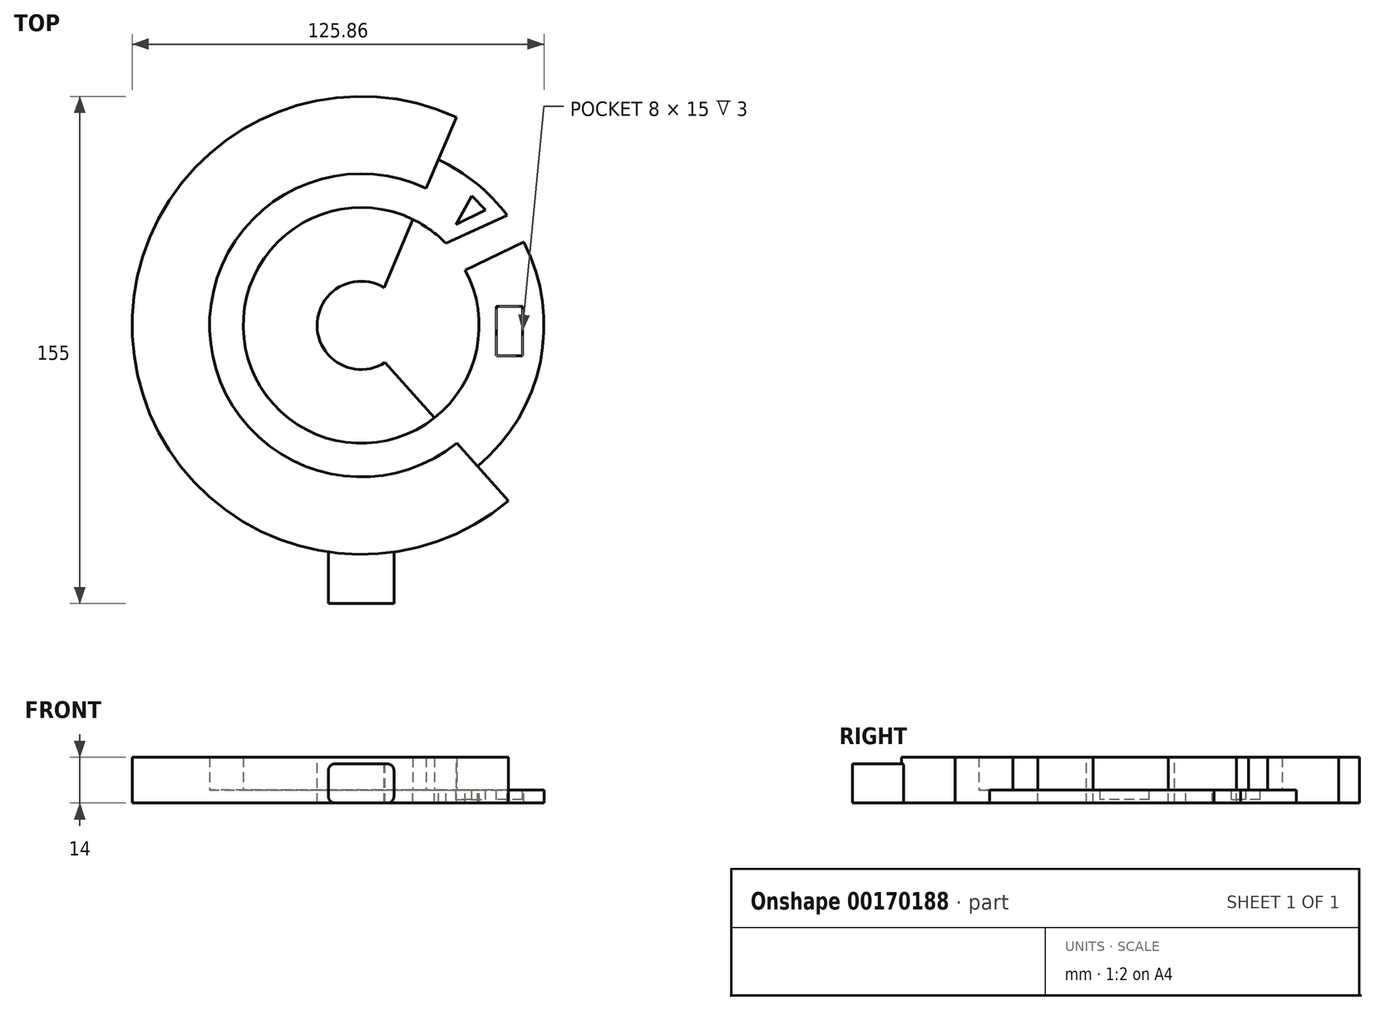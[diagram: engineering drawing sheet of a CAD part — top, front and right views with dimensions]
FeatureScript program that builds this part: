
annotation { "Feature Type Name" : "Feature", "Feature Type Description" : "" }
export const myFeature = defineFeature(function(context is Context, id is Id, definition is map)
    precondition{}
    {
        {
            var Q0;
            Q0=qCreatedBy(makeId("Top.planeOp"),FACE);
            var sketch = newSketch(context, id + "F0", { "sketchPlane" : qUnion([Q0])});
            skCircle(sketch, "E0", {"center": v(0, 0) * mm, "radius": 70 * mm});
            skCircle(sketch, "E1", {"center": v(0, 0) * mm, "radius": 46.34 * mm});
            skCircle(sketch, "E2", {"center": v(0, 0) * mm, "radius": 36.04 * mm});
            skCircle(sketch, "E3", {"center": v(0, 0) * mm, "radius": 13.49 * mm});
            skLineSegment(sketch, "E4", {"start": v(7.26, -11.37) * mm, "end": v(45, -53.62) * mm});
            skLineSegment(sketch, "E5", {"start": v(6.97, 11.55) * mm, "end": v(29.14, 63.65) * mm});
            skCircle(sketch, "E6", {"center": v(0, 0) * mm, "radius": 55.86 * mm});
            skCircle(sketch, "E7", {"center": v(0, 0) * mm, "radius": 32.82 * mm});
            skCircle(sketch, "E8", {"center": v(0, 0) * mm, "radius": 74.95 * mm});
            skLineSegment(sketch, "E9", {"start": v(26.8, -18.95) * mm, "end": v(42.53, -36.22) * mm});
            skLineSegment(sketch, "E10", {"start": v(49.72, 25.46) * mm, "end": v(28.92, 15.51) * mm});
            skLineSegment(sketch, "E11", {"start": v(22.75, 23.65) * mm, "end": v(40.37, 63.15) * mm});
            skLineSegment(sketch, "E12", {"start": v(22.75, 23.65) * mm, "end": v(62.3, 41.68) * mm});
            skLineSegment(sketch, "E13", {"start": v(0, -85) * mm, "end": v(0, -70) * mm});
            skLineSegment(sketch, "E14", {"start": v(0, -85) * mm, "end": v(10, -85) * mm});
            skLineSegment(sketch, "E15", {"start": v(0, -85) * mm, "end": v(-10, -85) * mm});
            skLineSegment(sketch, "E16", {"start": v(10, -85) * mm, "end": v(10, -69.28) * mm});
            skLineSegment(sketch, "E17", {"start": v(-10, -85) * mm, "end": v(-10, -69.28) * mm});
            skSolve(sketch);
        }
        {
            var Q0;
            {var subQ0=sQuery(id+"F0.wireOp",EDGE,"E4");var subQ1=sQuery(id+"F0.wireOp",EDGE,"E0");var subQ2=makeQuery(id+"F0.imprint","INTERSECT",VERTEX,{"derivedFrom":[subQ1,subQ0]});Q0=makeQuery(id+"F0.imprint","IMPRINT",FACE,{"disambiguationData":[TD([[makeQuery(id+"F0.imprint","IMPRINT",EDGE,{"disambiguationData":[TD([[subQ2,1.0]])],"derivedFrom":subQ1}),1.0]])]});}
            var Q1;
            {var subQ0=sQuery(id+"F0.wireOp",EDGE,"E5");var subQ1=sQuery(id+"F0.wireOp",EDGE,"E1");var subQ2=makeQuery(id+"F0.imprint","INTERSECT",VERTEX,{"derivedFrom":[subQ1,subQ0]});Q1=makeQuery(id+"F0.imprint","IMPRINT",FACE,{"disambiguationData":[TD([[makeQuery(id+"F0.imprint","IMPRINT",EDGE,{"disambiguationData":[TD([[subQ2,-1.0]])],"derivedFrom":subQ1}),-1.0]])]});}
            var Q2;
            {var subQ0=sQuery(id+"F0.wireOp",EDGE,"E5");var subQ1=sQuery(id+"F0.wireOp",EDGE,"E2");var subQ2=makeQuery(id+"F0.imprint","INTERSECT",VERTEX,{"derivedFrom":[subQ1,subQ0]});Q2=makeQuery(id+"F0.imprint","IMPRINT",FACE,{"disambiguationData":[TD([[makeQuery(id+"F0.imprint","IMPRINT",EDGE,{"disambiguationData":[TD([[subQ2,-1.0]])],"derivedFrom":subQ1}),1.0]])]});}
            var Q3;
            {var subQ0=sQuery(id+"F0.wireOp",EDGE,"E4");var subQ1=sQuery(id+"F0.wireOp",EDGE,"E3");var subQ2=makeQuery(id+"F0.imprint","INTERSECT",VERTEX,{"derivedFrom":[subQ1,subQ0]});Q3=makeQuery(id+"F0.imprint","IMPRINT",FACE,{"disambiguationData":[TD([[makeQuery(id+"F0.imprint","IMPRINT",EDGE,{"disambiguationData":[TD([[subQ2,1.0]])],"derivedFrom":subQ1}),-1.0]])]});}
            var Q4;
            {var subQ0=sQuery(id+"F0.wireOp",EDGE,"E5");var subQ1=sQuery(id+"F0.wireOp",EDGE,"E1");var subQ2=makeQuery(id+"F0.imprint","INTERSECT",VERTEX,{"derivedFrom":[subQ1,subQ0]});Q4=makeQuery(id+"F0.imprint","IMPRINT",FACE,{"disambiguationData":[TD([[makeQuery(id+"F0.imprint","IMPRINT",EDGE,{"disambiguationData":[TD([[subQ2,-1.0]])],"derivedFrom":subQ1}),1.0]])]});}
            var Q5;
            {var subQ0=sQuery(id+"F0.wireOp",EDGE,"E11");var subQ1=sQuery(id+"F0.wireOp",EDGE,"E1");var subQ2=makeQuery(id+"F0.imprint","INTERSECT",VERTEX,{"derivedFrom":[subQ1,subQ0]});Q5=makeQuery(id+"F0.imprint","IMPRINT",FACE,{"disambiguationData":[TD([[makeQuery(id+"F0.imprint","IMPRINT",EDGE,{"disambiguationData":[TD([[subQ2,-1.0]])],"derivedFrom":subQ1}),-1.0]])]});}
            var Q6;
            {var subQ0=sQuery(id+"F0.wireOp",EDGE,"E11");var subQ1=sQuery(id+"F0.wireOp",EDGE,"E1");var subQ2=makeQuery(id+"F0.imprint","INTERSECT",VERTEX,{"derivedFrom":[subQ1,subQ0]});Q6=makeQuery(id+"F0.imprint","IMPRINT",FACE,{"disambiguationData":[TD([[makeQuery(id+"F0.imprint","IMPRINT",EDGE,{"disambiguationData":[TD([[subQ2,-1.0]])],"derivedFrom":subQ1}),1.0]])]});}
            var Q7;
            {var subQ0=sQuery(id+"F0.wireOp",EDGE,"E12");var subQ1=sQuery(id+"F0.wireOp",EDGE,"E1");var subQ2=makeQuery(id+"F0.imprint","INTERSECT",VERTEX,{"derivedFrom":[subQ1,subQ0]});Q7=makeQuery(id+"F0.imprint","IMPRINT",FACE,{"disambiguationData":[TD([[makeQuery(id+"F0.imprint","IMPRINT",EDGE,{"disambiguationData":[TD([[subQ2,-1.0]])],"derivedFrom":subQ1}),1.0]])]});}
            var Q8;
            {var subQ0=sQuery(id+"F0.wireOp",EDGE,"E12");var subQ1=sQuery(id+"F0.wireOp",EDGE,"E1");var subQ2=makeQuery(id+"F0.imprint","INTERSECT",VERTEX,{"derivedFrom":[subQ1,subQ0]});Q8=makeQuery(id+"F0.imprint","IMPRINT",FACE,{"disambiguationData":[TD([[makeQuery(id+"F0.imprint","IMPRINT",EDGE,{"disambiguationData":[TD([[subQ2,-1.0]])],"derivedFrom":subQ1}),-1.0]])]});}
            var Q9;
            {var subQ0=sQuery(id+"F0.wireOp",EDGE,"E4");var subQ1=sQuery(id+"F0.wireOp",EDGE,"E1");var subQ2=makeQuery(id+"F0.imprint","INTERSECT",VERTEX,{"derivedFrom":[subQ1,subQ0]});Q9=makeQuery(id+"F0.imprint","IMPRINT",FACE,{"disambiguationData":[TD([[makeQuery(id+"F0.imprint","IMPRINT",EDGE,{"disambiguationData":[TD([[subQ2,-1.0]])],"derivedFrom":subQ1}),1.0]])]});}
            var Q10;
            {var subQ0=sQuery(id+"F0.wireOp",EDGE,"E4");var subQ1=sQuery(id+"F0.wireOp",EDGE,"E1");var subQ2=makeQuery(id+"F0.imprint","INTERSECT",VERTEX,{"derivedFrom":[subQ1,subQ0]});Q10=makeQuery(id+"F0.imprint","IMPRINT",FACE,{"disambiguationData":[TD([[makeQuery(id+"F0.imprint","IMPRINT",EDGE,{"disambiguationData":[TD([[subQ2,-1.0]])],"derivedFrom":subQ1}),-1.0]])]});}
            var Q11;
            {var subQ0=sQuery(id+"F0.wireOp",EDGE,"E10");var subQ1=sQuery(id+"F0.wireOp",EDGE,"E1");var subQ2=makeQuery(id+"F0.imprint","INTERSECT",VERTEX,{"derivedFrom":[subQ1,subQ0]});Q11=makeQuery(id+"F0.imprint","IMPRINT",FACE,{"disambiguationData":[TD([[makeQuery(id+"F0.imprint","IMPRINT",EDGE,{"disambiguationData":[TD([[subQ2,1.0]])],"derivedFrom":subQ1}),-1.0]])]});}
            var Q12;
            {var subQ0=sQuery(id+"F0.wireOp",EDGE,"E10");var subQ1=sQuery(id+"F0.wireOp",EDGE,"E1");var subQ2=makeQuery(id+"F0.imprint","INTERSECT",VERTEX,{"derivedFrom":[subQ1,subQ0]});Q12=makeQuery(id+"F0.imprint","IMPRINT",FACE,{"disambiguationData":[TD([[makeQuery(id+"F0.imprint","IMPRINT",EDGE,{"disambiguationData":[TD([[subQ2,1.0]])],"derivedFrom":subQ1}),1.0]])]});}
            extrude(context, id + "F1", {"entities" : qUnion([Q0, Q1, Q2, Q3, Q4, Q5, Q6, Q7, Q8, Q9, Q10, Q11, Q12]), "oppositeDirection" : true, "depth" : 4 * mm});
        }
        {
            var Q0;
            {var subQ0=sQuery(id+"F0.wireOp",EDGE,"E4");var subQ1=sQuery(id+"F0.wireOp",EDGE,"E0");var subQ2=makeQuery(id+"F0.imprint","INTERSECT",VERTEX,{"derivedFrom":[subQ1,subQ0]});Q0=makeQuery(id+"F0.imprint","IMPRINT",FACE,{"disambiguationData":[TD([[makeQuery(id+"F0.imprint","IMPRINT",EDGE,{"disambiguationData":[TD([[subQ2,1.0]])],"derivedFrom":subQ1}),1.0]])]});}
            var Q1;
            {var subQ0=sQuery(id+"F0.wireOp",EDGE,"E5");var subQ1=sQuery(id+"F0.wireOp",EDGE,"E1");var subQ2=makeQuery(id+"F0.imprint","INTERSECT",VERTEX,{"derivedFrom":[subQ1,subQ0]});Q1=makeQuery(id+"F0.imprint","IMPRINT",FACE,{"disambiguationData":[TD([[makeQuery(id+"F0.imprint","IMPRINT",EDGE,{"disambiguationData":[TD([[subQ2,-1.0]])],"derivedFrom":subQ1}),-1.0]])]});}
            var Q2;
            {var subQ0=sQuery(id+"F0.wireOp",EDGE,"E4");var subQ1=sQuery(id+"F0.wireOp",EDGE,"E3");var subQ2=makeQuery(id+"F0.imprint","INTERSECT",VERTEX,{"derivedFrom":[subQ1,subQ0]});Q2=makeQuery(id+"F0.imprint","IMPRINT",FACE,{"disambiguationData":[TD([[makeQuery(id+"F0.imprint","IMPRINT",EDGE,{"disambiguationData":[TD([[subQ2,1.0]])],"derivedFrom":subQ1}),-1.0]])]});}
            var Q3;
            {var subQ0=sQuery(id+"F0.wireOp",EDGE,"E5");var subQ1=sQuery(id+"F0.wireOp",EDGE,"E2");var subQ2=makeQuery(id+"F0.imprint","INTERSECT",VERTEX,{"derivedFrom":[subQ1,subQ0]});Q3=makeQuery(id+"F0.imprint","IMPRINT",FACE,{"disambiguationData":[TD([[makeQuery(id+"F0.imprint","IMPRINT",EDGE,{"disambiguationData":[TD([[subQ2,-1.0]])],"derivedFrom":subQ1}),1.0]])]});}
            extrude(context, id + "F2", {"entities" : qUnion([Q0, Q1, Q2, Q3]), "operationType" : NewBodyOperationType.ADD, "depth" : 10 * mm});
        }
        {
            var Q0;
            {var subQ0=sQuery(id+"F0.wireOp",EDGE,"E12");var subQ1=sQuery(id+"F0.wireOp",EDGE,"E1");var subQ2=makeQuery(id+"F0.imprint","INTERSECT",VERTEX,{"derivedFrom":[subQ1,subQ0]});Q0=makeQuery(id+"F0.imprint","IMPRINT",FACE,{"disambiguationData":[TD([[makeQuery(id+"F0.imprint","IMPRINT",EDGE,{"disambiguationData":[TD([[subQ2,-1.0]])],"derivedFrom":subQ1}),-1.0]])]});}
            var sketch = newSketch(context, id + "F3", { "sketchPlane" : qUnion([Q0])});
            skLineSegment(sketch, "E18", {"start": v(33.85, 39.63) * mm, "end": v(29, 30.88) * mm});
            skLineSegment(sketch, "E19", {"start": v(29, 30.88) * mm, "end": v(37.99, 35.28) * mm});
            skLineSegment(sketch, "E20", {"start": v(33.85, 39.63) * mm, "end": v(37.99, 35.28) * mm});
            skLineSegment(sketch, "E21", {"start": v(41.27, 5.75) * mm, "end": v(41.27, -9.25) * mm});
            skLineSegment(sketch, "E22", {"start": v(41.27, -9.25) * mm, "end": v(49.27, -9.25) * mm});
            skLineSegment(sketch, "E23", {"start": v(49.27, -9.25) * mm, "end": v(49.27, 5.75) * mm});
            skLineSegment(sketch, "E24", {"start": v(49.27, 5.75) * mm, "end": v(41.27, 5.75) * mm});
            skSolve(sketch);
        }
        {
            var Q0;
            Q0 = qSketchRegion(id + "F3", true);
            extrude(context, id + "F4", {"entities" : qUnion([Q0]), "operationType" : NewBodyOperationType.REMOVE, "oppositeDirection" : true, "depth" : 3 * mm});
        }
        {
            var Q0;
            {var subQ0=sQuery(id+"F0.wireOp",EDGE,"E13");var subQ1=sQuery(id+"F0.wireOp",EDGE,"E0");var subQ2=makeQuery(id+"F0.imprint","INTERSECT",VERTEX,{"derivedFrom":[subQ1,subQ0]});Q0=makeQuery(id+"F0.imprint","IMPRINT",FACE,{"disambiguationData":[TD([[makeQuery(id+"F0.imprint","IMPRINT",EDGE,{"disambiguationData":[TD([[subQ2,1.0]])],"derivedFrom":subQ1}),-1.0]])]});}
            var Q1;
            {var subQ0=sQuery(id+"F0.wireOp",EDGE,"E13");var subQ1=sQuery(id+"F0.wireOp",EDGE,"E0");var subQ2=makeQuery(id+"F0.imprint","INTERSECT",VERTEX,{"derivedFrom":[subQ1,subQ0]});Q1=makeQuery(id+"F0.imprint","IMPRINT",FACE,{"disambiguationData":[TD([[makeQuery(id+"F0.imprint","IMPRINT",EDGE,{"disambiguationData":[TD([[subQ2,-1.0]])],"derivedFrom":subQ1}),-1.0]])]});}
            var Q2;
            {var subQ5=sQuery(id+"F0.wireOp",EDGE,"E14");Q2=makeQuery(id+"F0.imprint","IMPRINT",FACE,{"disambiguationData":[TD([[makeQuery(id+"F0.imprint","IMPRINT",EDGE,{"derivedFrom":subQ5}),1.0]])]});}
            var Q3;
            {var subQ5=sQuery(id+"F0.wireOp",EDGE,"E15");Q3=makeQuery(id+"F0.imprint","IMPRINT",FACE,{"disambiguationData":[TD([[makeQuery(id+"F0.imprint","IMPRINT",EDGE,{"derivedFrom":subQ5}),-1.0]])]});}
            extrude(context, id + "F5", {"entities" : qUnion([Q0, Q1, Q2, Q3]), "operationType" : NewBodyOperationType.ADD, "oppositeDirection" : true, "depth" : 4 * mm});
        }
        {
            var Q0;
            {var subQ0=sQuery(id+"F0.wireOp",EDGE,"E13");var subQ1=sQuery(id+"F0.wireOp",EDGE,"E0");var subQ2=makeQuery(id+"F0.imprint","INTERSECT",VERTEX,{"derivedFrom":[subQ1,subQ0]});Q0=makeQuery(id+"F0.imprint","IMPRINT",FACE,{"disambiguationData":[TD([[makeQuery(id+"F0.imprint","IMPRINT",EDGE,{"disambiguationData":[TD([[subQ2,1.0]])],"derivedFrom":subQ1}),-1.0]])]});}
            var Q1;
            {var subQ5=sQuery(id+"F0.wireOp",EDGE,"E15");Q1=makeQuery(id+"F0.imprint","IMPRINT",FACE,{"disambiguationData":[TD([[makeQuery(id+"F0.imprint","IMPRINT",EDGE,{"derivedFrom":subQ5}),-1.0]])]});}
            var Q2;
            {var subQ0=sQuery(id+"F0.wireOp",EDGE,"E13");var subQ1=sQuery(id+"F0.wireOp",EDGE,"E0");var subQ2=makeQuery(id+"F0.imprint","INTERSECT",VERTEX,{"derivedFrom":[subQ1,subQ0]});Q2=makeQuery(id+"F0.imprint","IMPRINT",FACE,{"disambiguationData":[TD([[makeQuery(id+"F0.imprint","IMPRINT",EDGE,{"disambiguationData":[TD([[subQ2,-1.0]])],"derivedFrom":subQ1}),-1.0]])]});}
            var Q3;
            {var subQ5=sQuery(id+"F0.wireOp",EDGE,"E14");Q3=makeQuery(id+"F0.imprint","IMPRINT",FACE,{"disambiguationData":[TD([[makeQuery(id+"F0.imprint","IMPRINT",EDGE,{"derivedFrom":subQ5}),1.0]])]});}
            extrude(context, id + "F6", {"entities" : qUnion([Q0, Q1, Q2, Q3]), "operationType" : NewBodyOperationType.ADD, "depth" : 8 * mm});
        }
        {
            var Q0;
            Q0=makeQuery(id+"F6.opExtrude","CAP_EDGE",EDGE,{"disambiguationData":[OSD([sQuery(id+"F0.wireOp",EDGE,"E16")])],"isStart":false});
            var Q1;
            Q1=makeQuery(id+"F6.opExtrude","CAP_EDGE",EDGE,{"disambiguationData":[OSD([sQuery(id+"F0.wireOp",EDGE,"E17")])],"isStart":false});
            var Q2;
            Q2=makeQuery(id+"F5.opExtrude","CAP_EDGE",EDGE,{"disambiguationData":[OSD([sQuery(id+"F0.wireOp",EDGE,"E16")])],"isStart":false});
            var Q3;
            Q3=makeQuery(id+"F5.opExtrude","CAP_EDGE",EDGE,{"disambiguationData":[OSD([sQuery(id+"F0.wireOp",EDGE,"E17")])],"isStart":false});
            fillet(context, id + "F7", {"entities" : qUnion([Q0, Q1, Q2, Q3]), "radius" : 2 * mm, "tangentPropagation" : true, "allowEdgeOverflow" : false});
        }
    });
